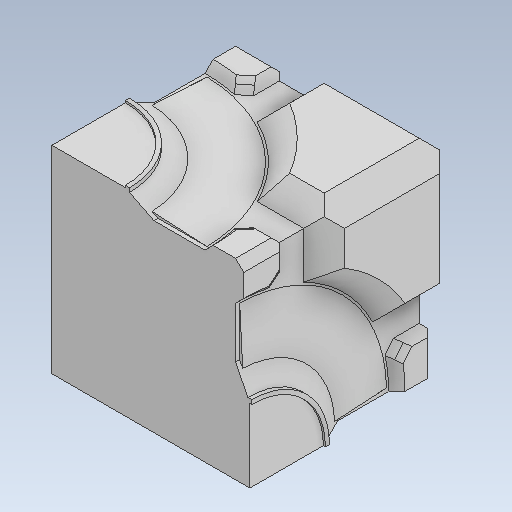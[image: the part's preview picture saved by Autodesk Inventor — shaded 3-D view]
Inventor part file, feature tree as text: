
AUTODESK INVENTOR PART (.ipt)
format: ipt  version: 2020 (Build 240168000, 168)  size: 339,456 bytes
history: native  units: in
note: dims shown in document units (in); Inventor stores cm internally (conversion verified against a paired STEP export)
features: sketch x12, other x3
ambient origin geometry x8: Origin, YZ Plane, XZ Plane, XY Plane, X Axis, Y Axis, Z Axis, Center Point
bodies: Solid1 (feature_tree)
feature tree (15):
  other  "Portal Companion Cube.ipt"
  other  "Solid1::Portal Companion Cube.ipt"
  other  "TaggingFeature1"
  sketch  "Sketch1"  dims[d0=0.3937in]
  sketch  "Sketch2"
  sketch  "Sketch3"
  sketch  "Sketch4"
  sketch  "Sketch5"
  sketch  "Sketch7"
  sketch  "Sketch8"
  sketch  "Sketch9"
  sketch  "Sketch10"
  sketch  "Sketch13"
  sketch  "Sketch14"
  sketch  "Sketch15"
